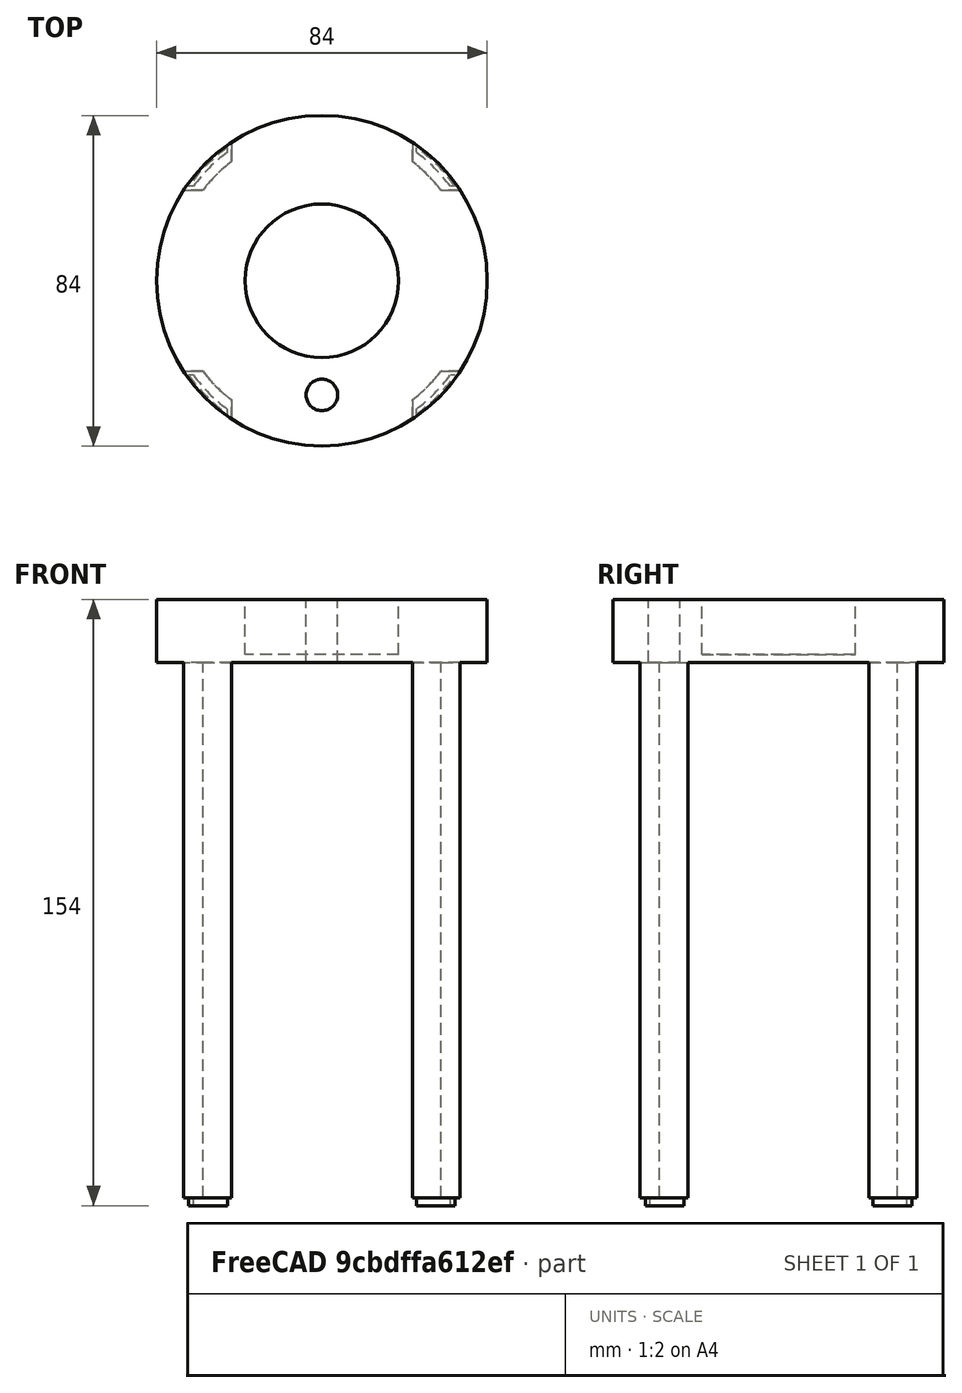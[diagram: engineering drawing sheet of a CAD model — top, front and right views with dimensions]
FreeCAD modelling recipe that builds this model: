
FCSTD DOCUMENT  (FreeCAD 0.18R4 (GitTag))
Label: 2
License: All rights reserved
LicenseURL: http://en.wikipedia.org/wiki/All_rights_reserved
objects: Part::Cut×10, Part::Cylinder×7, Part::Box×4
note: 21 computed .brp shape members not serialized (recipe doc carries the construction recipe); baked Part::Feature solids carry a one-line shape summary decoded from their .brp

FEATURE [Part::Cylinder] Cylinder  label="Base"
  Angle = 360
  AttacherType = Attacher::AttachEngine3D
  Height = 154
  Placement = pos=(0,0,-2) rot=(0,0,1;0rad)
  Radius = 42
FEATURE [Part::Cylinder] Cylinder001  label="Agujero superior"
  Angle = 360
  AttacherType = Attacher::AttachEngine3D
  Height = 15
  Placement = pos=(0,0,138) rot=(0,0,1;0rad)
  Radius = 19.5
FEATURE [Part::Cut] Cut  label="Corte superior"
  Base = -> Cylinder
  Tool = -> Cylinder001
FEATURE [Part::Cylinder] Cylinder002  label="Agujero inferior"
  Angle = 360
  AttacherType = Attacher::AttachEngine3D
  Height = 138
  Placement = pos=(0,0,-2) rot=(0,0,1;0rad)
  Radius = 38
FEATURE [Part::Cut] Cut001  label="Corte inferior"
  Base = -> Cut
  Tool = -> Cylinder002
FEATURE [Part::Box] Box  label="Cubo"
  AttacherType = Attacher::AttachEngine3D
  Height = 138
  Length = 46
  Placement = pos=(-23,-50,-2) rot=(0,0,1;0rad)
  Width = 99
FEATURE [Part::Box] Box001  label="Cubo001"
  AttacherType = Attacher::AttachEngine3D
  Height = 138
  Length = 46
  Placement = pos=(44,-23,-2) rot=(0,0,1;1.5708rad)
  Width = 99
FEATURE [Part::Cut] Cut002
  Base = -> Cut001
  Tool = -> Box
FEATURE [Part::Cut] Cut003
  Base = -> Cut002
  Tool = -> Box001
FEATURE [Part::Cylinder] Cylinder003  label="Agujero cables"
  Angle = 360
  AttacherType = Attacher::AttachEngine3D
  Height = 26
  Placement = pos=(0,-29,131) rot=(0,0,1;0rad)
  Radius = 4
FEATURE [Part::Cut] Cut004
  Base = -> Cut003
  Tool = -> Cylinder003
FEATURE [Part::Cylinder] Cylinder004  label="Agujero inferior001"
  Angle = 360
  AttacherType = Attacher::AttachEngine3D
  Height = 2
  Placement = pos=(0,0,-2) rot=(0,0,1;0rad)
  Radius = 40.5
FEATURE [Part::Cut] Cut005
  Base = -> Cut004
  Tool = -> Cylinder004
FEATURE [Part::Cylinder] Cylinder005  label="Base001"
  Angle = 360
  AttacherType = Attacher::AttachEngine3D
  Height = 2
  Placement = pos=(0,0,-2) rot=(0,0,1;0rad)
  Radius = 42
FEATURE [Part::Cylinder] Cylinder006  label="Base002"
  Angle = 360
  AttacherType = Attacher::AttachEngine3D
  Height = 2
  Placement = pos=(0,0,-2) rot=(0,0,1;0rad)
  Radius = 41.5
FEATURE [Part::Cut] Cut006
  Base = -> Cylinder005
  Tool = -> Cylinder006
FEATURE [Part::Cut] Cut007
  Base = -> Cut005
  Tool = -> Cut006
FEATURE [Part::Box] Box002  label="Cubo002"
  AttacherType = Attacher::AttachEngine3D
  Height = 2
  Length = 48
  Placement = pos=(-24,-39,-2) rot=(0,0,1;0rad)
  Width = 78
FEATURE [Part::Cut] Cut008
  Base = -> Cut007
  Tool = -> Box002
FEATURE [Part::Box] Box003  label="Cubo003"
  AttacherType = Attacher::AttachEngine3D
  Height = 2
  Length = 48
  Placement = pos=(37,-24,-2) rot=(0,0,1;1.5708rad)
  Width = 78
FEATURE [Part::Cut] Cut009
  Base = -> Cut008
  Tool = -> Box003
